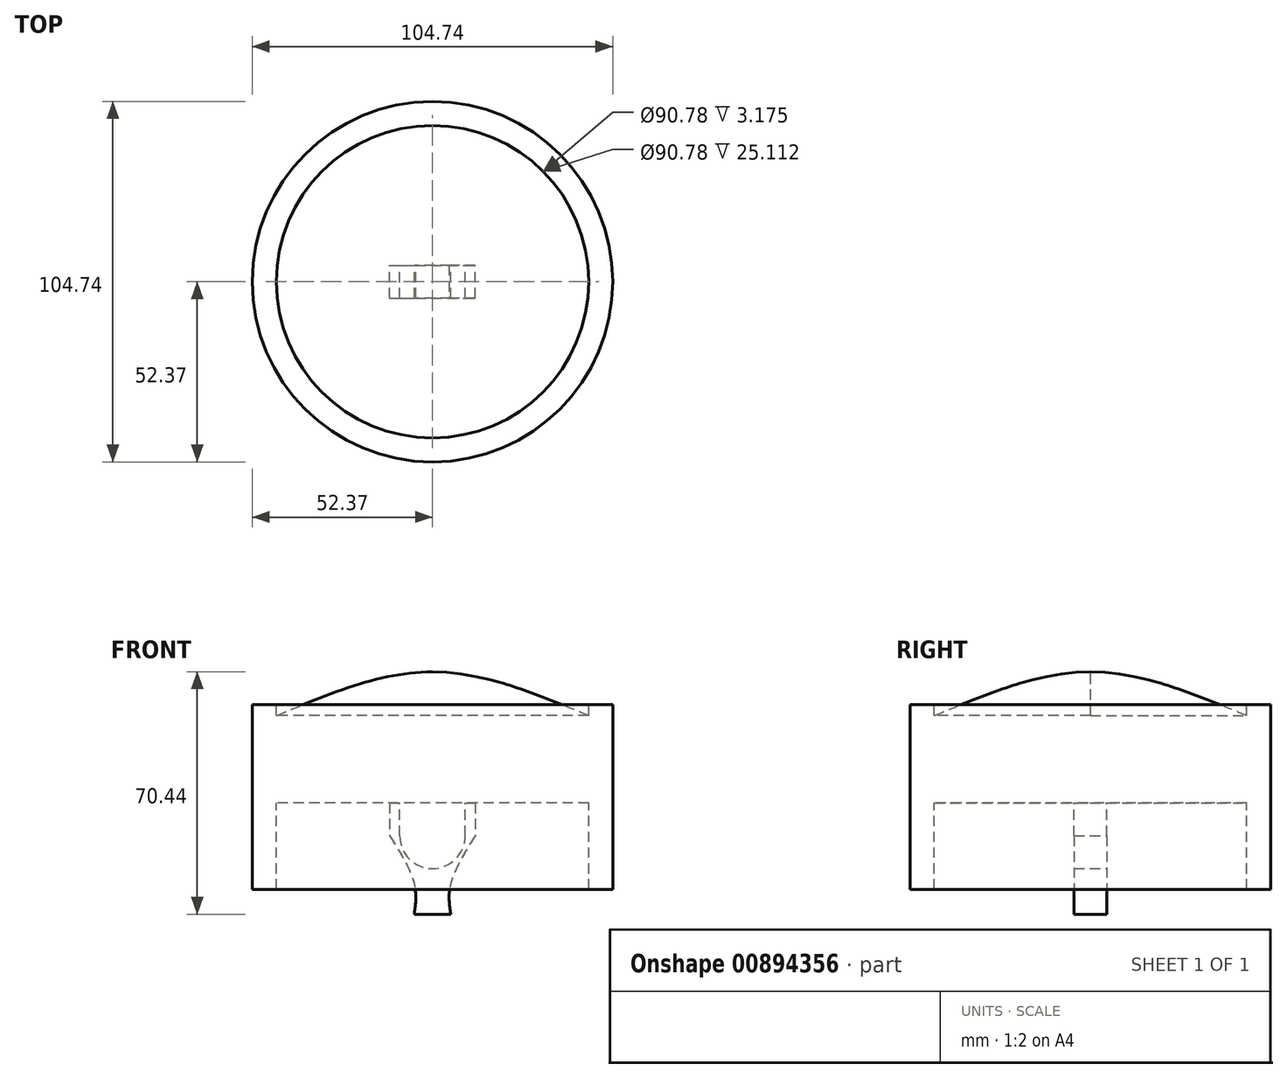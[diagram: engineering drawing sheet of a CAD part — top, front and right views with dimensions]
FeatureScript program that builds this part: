
annotation { "Feature Type Name" : "Feature", "Feature Type Description" : "" }
export const myFeature = defineFeature(function(context is Context, id is Id, definition is map)
    precondition{}
    {
        {
            var Q0;
            Q0=qCreatedBy(makeId("Front.planeOp"),FACE);
            var sketch = newSketch(context, id + "F0", { "sketchPlane" : qUnion([Q0])});
            skLineSegment(sketch, "E0.bottom", {"start": v(-45.39, 12.7) * mm, "end": v(45.39, 12.7) * mm});
            skLineSegment(sketch, "E0.top", {"start": v(-45.39, -12.7) * mm, "end": v(45.39, -12.7) * mm});
            skLineSegment(sketch, "E0.left", {"start": v(-45.39, 12.7) * mm, "end": v(-45.39, -12.7) * mm});
            skLineSegment(sketch, "E0.right", {"start": v(45.39, 12.7) * mm, "end": v(45.39, -12.7) * mm});
            skPoint(sketch, "E0.middle", {"position": v(0, 0) * mm});
            skFitSpline(sketch, "E1", {"points": [v(-45.39, 12.7) * mm, v(0, 25.43) * mm, v(45.39, 12.7) * mm], "startDerivative": vector(90.78, 37.5) * mm, "endDerivative": vector(90.78, -37.5) * mm});
            skLineSegment(sketch, "E2", {"start": v(-45.39, -12.7) * mm, "end": v(-52.37, -12.7) * mm});
            skLineSegment(sketch, "E3", {"start": v(-52.37, -12.7) * mm, "end": v(-52.37, 15.88) * mm});
            skLineSegment(sketch, "E4", {"start": v(-52.37, 15.88) * mm, "end": v(-45.39, 15.88) * mm});
            skLineSegment(sketch, "E5", {"start": v(-45.39, 15.88) * mm, "end": v(-45.39, 12.7) * mm});
            skLineSegment(sketch, "E6.bottom", {"start": v(45.39, -12.7) * mm, "end": v(39.04, -12.7) * mm});
            skLineSegment(sketch, "E7.bottom", {"start": v(-45.39, -12.7) * mm, "end": v(-39.04, -12.7) * mm});
            skLineSegment(sketch, "E7.left", {"start": v(-45.39, -12.7) * mm, "end": v(-45.39, -37.81) * mm});
            skLineSegment(sketch, "E8", {"start": v(0, 25.43) * mm, "end": v(0, -12.7) * mm});
            skLineSegment(sketch, "E9", {"start": v(-45.39, 12.7) * mm, "end": v(-45.39, 0) * mm});
            skLineSegment(sketch, "E10", {"start": v(0, -12.7) * mm, "end": v(0, -22.22) * mm});
            skCircle(sketch, "E11", {"center": v(0, -22.22) * mm, "radius": 9.52 * mm});
            skLineSegment(sketch, "E12", {"start": v(-9.52, -22.22) * mm, "end": v(-9.52, -12.7) * mm});
            skLineSegment(sketch, "E13", {"start": v(9.53, -22.22) * mm, "end": v(9.53, -12.7) * mm});
            skLineSegment(sketch, "E14", {"start": v(0, -45) * mm, "end": v(-5.3, -45) * mm});
            skLineSegment(sketch, "E15.MirrorCS", {"start": v(0, -45) * mm, "end": v(5.3, -45) * mm});
            skLineSegment(sketch, "E16.MirrorCS", {"start": v(9.52, -22.22) * mm, "end": v(9.52, -12.7) * mm});
            skLineSegment(sketch, "E17.bottom", {"start": v(-5.3, -45) * mm, "end": v(5.22, -45) * mm});
            skLineSegment(sketch, "E17.top", {"start": v(-5.3, -70.53) * mm, "end": v(5.22, -70.53) * mm});
            skLineSegment(sketch, "E17.left", {"start": v(-5.3, -45) * mm, "end": v(-5.3, -70.53) * mm});
            skLineSegment(sketch, "E17.right", {"start": v(5.22, -45) * mm, "end": v(5.22, -70.53) * mm});
            skLineSegment(sketch, "E18.left", {"start": v(-45.39, -20.78) * mm, "end": v(-45.39, -25.4) * mm});
            skLineSegment(sketch, "E19", {"start": v(-9.52, -12.7) * mm, "end": v(-12.41, -12.7) * mm, "construction": true});
            skLineSegment(sketch, "E20", {"start": v(-12.41, -12.7) * mm, "end": v(-12.41, -22.22) * mm});
            skFitSpline(sketch, "E21", {"points": [v(-12.41, -22.22) * mm, v(-5.28, -36.23) * mm, v(-5.3, -45) * mm], "startDerivative": vector(16.03, -25.6) * mm, "endDerivative": vector(-2.7, -19.69) * mm});
            skFitSpline(sketch, "E22.MirrorCS", {"points": [v(-12.41, -22.22) * mm, v(-5.28, -36.23) * mm, v(-5.3, -45) * mm], "startDerivative": vector(16.03, -25.6) * mm, "endDerivative": vector(-2.7, -19.69) * mm});
            skLineSegment(sketch, "E23.MirrorCS", {"start": v(12.41, -12.7) * mm, "end": v(12.41, -22.22) * mm});
            skFitSpline(sketch, "E24.MirrorCS", {"points": [v(12.41, -22.22) * mm, v(5.28, -36.23) * mm, v(5.3, -45) * mm], "startDerivative": vector(-16.03, -25.6) * mm, "endDerivative": vector(2.7, -19.69) * mm});
            skLineSegment(sketch, "E25", {"start": v(-52.37, -12.7) * mm, "end": v(-52.37, -37.81) * mm});
            skLineSegment(sketch, "E26", {"start": v(-52.37, -37.81) * mm, "end": v(-45.39, -37.81) * mm});
            skCircle(sketch, "E27", {"center": v(0, -22.22) * mm, "radius": 5.3 * mm});
            skSolve(sketch);
        }
        {
            var Q0;
            {var subQ0=sQuery(id+"F0.wireOp",EDGE,"E1");var subQ3=sQuery(id+"F0.wireOp",EDGE,"E8");var subQ5=makeQuery(id+"F0.imprint","INTERSECT",VERTEX,{"derivedFrom":[subQ0,subQ3]});Q0=makeQuery(id+"F0.imprint","IMPRINT",FACE,{"disambiguationData":[TD([[makeQuery(id+"F0.imprint","IMPRINT",EDGE,{"disambiguationData":[TD([[subQ5,-1.0]])],"derivedFrom":subQ3}),-1.0]])]});}
            var Q1;
            Q1=makeQuery(id+"F0.imprint","IMPRINT",FACE,{"disambiguationData":[TD([[makeQuery(id+"F0.imprint","IMPRINT",EDGE,{"derivedFrom":sQuery(id+"F0.wireOp",EDGE,"E0.left")}),-1.0]])]});
            var Q2;
            {var subQ4=sQuery(id+"F0.wireOp",EDGE,"E0.left");Q2=makeQuery(id+"F0.imprint","IMPRINT",FACE,{"disambiguationData":[TD([[makeQuery(id+"F0.imprint","IMPRINT",EDGE,{"derivedFrom":subQ4}),1.0]])]});}
            var Q3;
            Q3=makeQuery(id+"F0.imprint","IMPRINT",FACE,{"disambiguationData":[TD([[makeQuery(id+"F0.imprint","IMPRINT",EDGE,{"derivedFrom":sQuery(id+"F0.wireOp",EDGE,"E7.bottom")}),-1.0]])]});
            var Q4;
            Q4=sQuery(id+"F0.wireOp",EDGE,"E8");
            revolve(context, id + "F1", {"surfaceOperationType" : NewSurfaceOperationType.NEW, "entities" : qUnion([Q0, Q1, Q2, Q3]), "axis" : qUnion([Q4]), "revolveType" : RevolveType.FULL});
        }
        {
            var Q0;
            Q0=makeQuery(id+"F0.imprint","IMPRINT",FACE,{"disambiguationData":[TD([[makeQuery(id+"F0.imprint","IMPRINT",EDGE,{"derivedFrom":sQuery(id+"F0.wireOp",EDGE,"E0.left")}),1.0]])]});
            var Q1;
            {var subQ0=sQuery(id+"F0.wireOp",EDGE,"E1");var subQ3=sQuery(id+"F0.wireOp",EDGE,"E8");var subQ5=makeQuery(id+"F0.imprint","INTERSECT",VERTEX,{"derivedFrom":[subQ0,subQ3]});Q1=makeQuery(id+"F0.imprint","IMPRINT",FACE,{"disambiguationData":[TD([[makeQuery(id+"F0.imprint","IMPRINT",EDGE,{"disambiguationData":[TD([[subQ5,-1.0]])],"derivedFrom":subQ3}),-1.0]])]});}
            var Q2;
            Q2=makeQuery(id+"F0.imprint","IMPRINT",FACE,{"disambiguationData":[TD([[makeQuery(id+"F0.imprint","IMPRINT",EDGE,{"derivedFrom":sQuery(id+"F0.wireOp",EDGE,"E7.bottom")}),-1.0]])]});
            var Q3;
            Q3=makeQuery(id+"F0.imprint","IMPRINT",FACE,{"disambiguationData":[TD([[makeQuery(id+"F0.imprint","IMPRINT",EDGE,{"derivedFrom":sQuery(id+"F0.wireOp",EDGE,"E0.left")}),-1.0]])]});
            var Q4;
            Q4=makeQuery(id+"F0.imprint","IMPRINT",FACE,{"disambiguationData":[TD([[makeQuery(id+"F0.imprint","IMPRINT",EDGE,{"derivedFrom":sQuery(id+"F0.wireOp",EDGE,"E18.bottom")}),1.0]])]});
            var Q5;
            Q5=sQuery(id+"F0.wireOp",EDGE,"E8");
            revolve(context, id + "F2", {"operationType" : NewBodyOperationType.ADD, "surfaceOperationType" : NewSurfaceOperationType.NEW, "entities" : qUnion([Q0, Q1, Q2, Q3, Q4]), "axis" : qUnion([Q5]), "revolveType" : RevolveType.FULL});
        }
        {
            var Q0;
            {var subQ0=sQuery(id+"F0.wireOp",EDGE,"E1");var subQ3=sQuery(id+"F0.wireOp",EDGE,"E8");var subQ5=makeQuery(id+"F0.imprint","INTERSECT",VERTEX,{"derivedFrom":[subQ0,subQ3]});Q0=makeQuery(id+"F0.imprint","IMPRINT",FACE,{"disambiguationData":[TD([[makeQuery(id+"F0.imprint","IMPRINT",EDGE,{"disambiguationData":[TD([[subQ5,-1.0]])],"derivedFrom":subQ3}),-1.0]])]});}
            var Q1;
            Q1=makeQuery(id+"F0.imprint","IMPRINT",FACE,{"disambiguationData":[TD([[makeQuery(id+"F0.imprint","IMPRINT",EDGE,{"derivedFrom":sQuery(id+"F0.wireOp",EDGE,"E0.left")}),1.0]])]});
            var Q2;
            Q2=makeQuery(id+"F0.imprint","IMPRINT",FACE,{"disambiguationData":[TD([[makeQuery(id+"F0.imprint","IMPRINT",EDGE,{"derivedFrom":sQuery(id+"F0.wireOp",EDGE,"E7.bottom")}),-1.0]])]});
            var Q3;
            Q3=makeQuery(id+"F0.imprint","IMPRINT",FACE,{"disambiguationData":[TD([[makeQuery(id+"F0.imprint","IMPRINT",EDGE,{"derivedFrom":sQuery(id+"F0.wireOp",EDGE,"E0.left")}),-1.0]])]});
            var Q4;
            Q4=sQuery(id+"F0.wireOp",EDGE,"E8");
            revolve(context, id + "F3", {"operationType" : NewBodyOperationType.ADD, "surfaceOperationType" : NewSurfaceOperationType.NEW, "entities" : qUnion([Q0, Q1, Q2, Q3]), "axis" : qUnion([Q4]), "revolveType" : RevolveType.FULL});
        }
        {
            var Q0;
            Q0=sQuery(id+"F0.wireOp",EDGE,"E11");
            var Q1;
            Q1=sQuery(id+"F0.wireOp",EDGE,"E27");
            extrude(context, id + "F4", {"bodyType" : ToolBodyType.SURFACE, "surfaceEntities" : qUnion([Q0, Q1]), "endBound" : BoundingType.SYMMETRIC, "depth" : 93.01 * mm, "offsetDistance" : 25.4 * mm});
        }
        {
            var Q0;
            Q0=makeQuery(id+"F0.imprint","IMPRINT",FACE,{"disambiguationData":[TD([[makeQuery(id+"F0.imprint","IMPRINT",EDGE,{"derivedFrom":sQuery(id+"F0.wireOp",EDGE,"E17.bottom")}),-1.0]])]});
            var Q1;
            {var subQ3=sQuery(id+"F0.wireOp",EDGE,"E12");Q1=makeQuery(id+"F0.imprint","IMPRINT",FACE,{"disambiguationData":[TD([[makeQuery(id+"F0.imprint","IMPRINT",EDGE,{"derivedFrom":subQ3}),1.0]])]});}
            extrude(context, id + "F5", {"entities" : qUnion([Q0, Q1]), "endBound" : BoundingType.SYMMETRIC, "depth" : 9.52 * mm, "offsetDistance" : 25.4 * mm});
        }
        {
            var Q0;
            {var subQ3=sQuery(id+"F0.wireOp",EDGE,"E2");Q0=makeQuery(id+"F0.imprint","IMPRINT",FACE,{"disambiguationData":[TD([[makeQuery(id+"F0.imprint","IMPRINT",EDGE,{"derivedFrom":subQ3}),1.0]])]});}
            var Q1;
            Q1=sQuery(id+"F0.wireOp",EDGE,"E10");
            revolve(context, id + "F6", {"operationType" : NewBodyOperationType.ADD, "surfaceOperationType" : NewSurfaceOperationType.NEW, "entities" : qUnion([Q0]), "axis" : qUnion([Q1]), "revolveType" : RevolveType.FULL});
        }
    });
